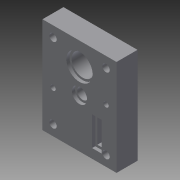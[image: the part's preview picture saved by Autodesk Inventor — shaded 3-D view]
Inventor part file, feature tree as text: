
AUTODESK INVENTOR PART (.ipt)
format: ipt  version: 2015 (Build 190159000, 159)  size: 151,040 bytes
history: native  units: mm
features: extrude x2, hole x2, sketch x2
ambient origin geometry x8: Origin, YZ Plane, XZ Plane, XY Plane, X Axis, Y Axis, Z Axis, Center Point
bodies: Solid1 (feature_tree)
feature tree (6):
  extrude  "Extrusion1"  Depth=23.5mm
  hole  "Hole1"  [1 undecoded]
  hole  "Hole2"  [1 undecoded]
  extrude  "Extrusion2"  Depth=5.0mm
  sketch  "Sketch1"  dims[d0=21.0mm d1=23.5mm]
  sketch  "Sketch2"  dims[d2=10.5mm d3=11.75mm d5=23.5mm d6=5.0mm d7=23.5mm d9=70.5mm d40=21.625mm d41=70.5mm d42=91.5mm d43=10.0mm d44=10.0mm d45=7.0mm d46=10.0mm d47=10.0mm d48=90.0deg d50=7.0mm d51=10.0mm d52=10.0mm d53=7.0mm d54=10.0mm d55=10.0mm d56=7.0mm d60=30.0mm d61=30.0mm d62=5.0mm d63=5.0mm d64=14.0mm d65=20.0mm d66=0.0mm d67=10.0mm d68=10.0mm d69=3.0mm d70=6.0mm d71=25.0mm d72=3.0mm d73=90.0deg d74=8.0mm d75=20.594885mm d76=10.0mm d77=10.0mm d78=3.0mm d79=6.0mm d80=14.5mm d81=3.0mm d82=90.0deg d83=8.0mm d84=20.594885mm d85=33.25mm d86=12.0mm d87=9.0mm d88=27.75mm d89=3.0mm d90=0.0mm]
note: 2 required parameter values undecoded (feature->parameter linkage not recoverable at this tier; creation-order binding heuristic only, values carry confidence <= 0.55)
